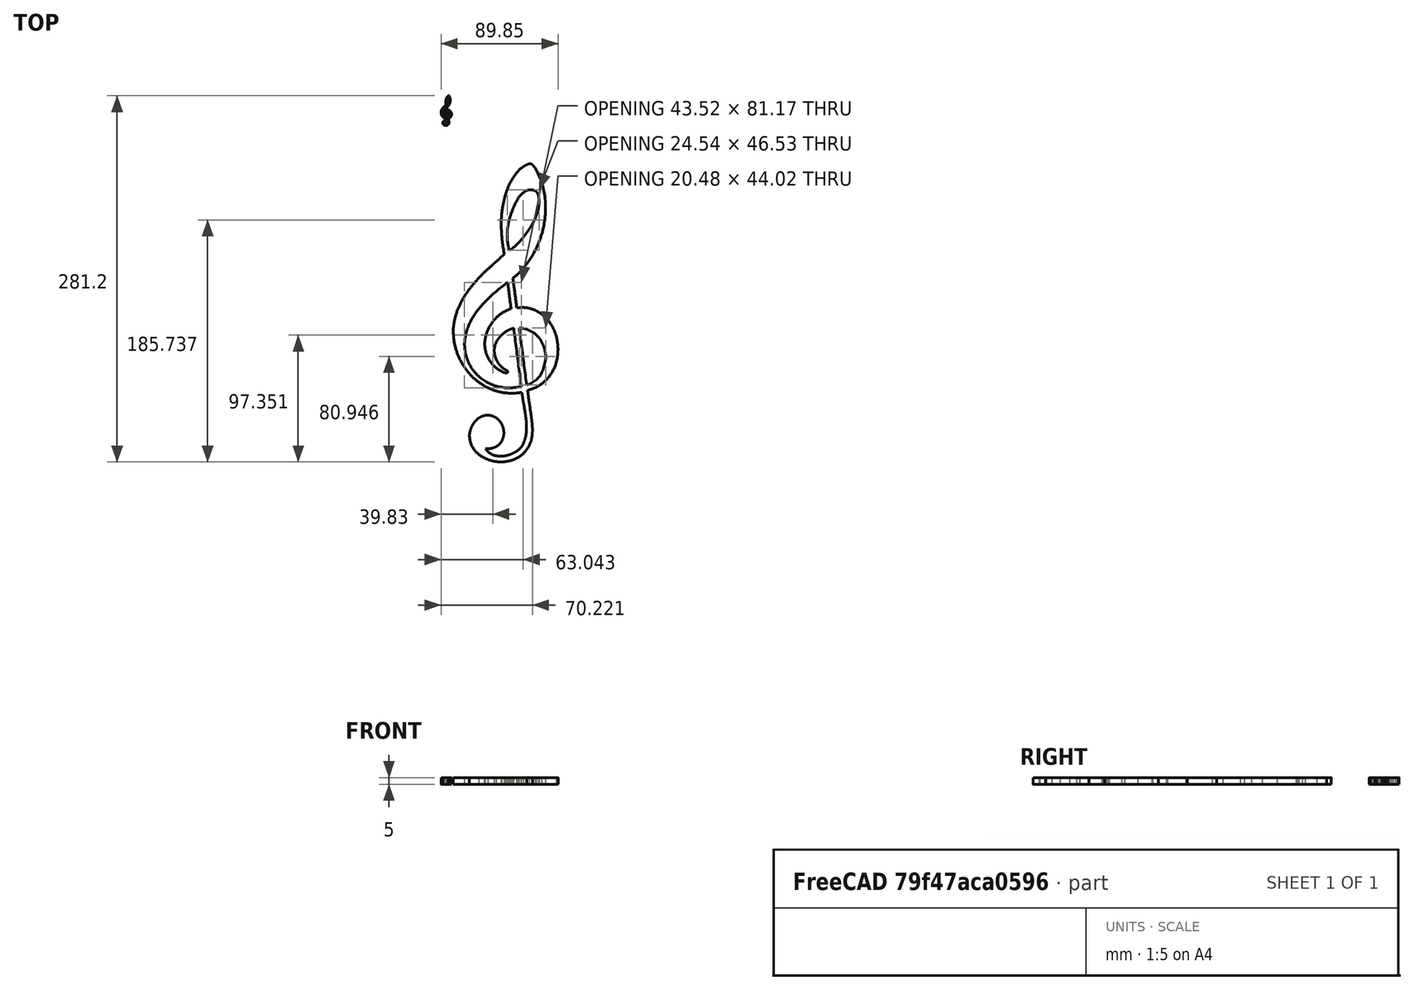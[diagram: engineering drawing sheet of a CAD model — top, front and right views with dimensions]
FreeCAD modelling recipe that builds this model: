
FCSTD DOCUMENT  (FreeCAD 0.17R13541 (Git))
Label: ClefdeSol
License: All rights reserved
LicenseURL: http://en.wikipedia.org/wiki/All_rights_reserved
objects: Part::Feature×4, Sketcher::SketchObject×2, Part::Part2DObjectPython×2, PartDesign::FeatureBase×1, PartDesign::Pad×1, PartDesign::Body×1, App::DocumentObjectGroup×1, Part::FeaturePython×1
note: 13 computed .brp shape members not serialized (recipe doc carries the construction recipe); baked Part::Feature solids carry a one-line shape summary decoded from their .brp

FEATURE [Part::Feature] path9
  shape: bbox 43.66 x 81.18 x 2e-07 mm, 1 faces, 0 solids (baked)
FEATURE [Part::Feature] path9001
  shape: bbox 20.48 x 44.02 x 2e-07 mm, 1 faces, 0 solids (baked)
FEATURE [Part::Feature] path9002
  shape: bbox 24.68 x 46.76 x 2e-07 mm, 1 faces, 0 solids (baked)
FEATURE [Part::Feature] path9003
  shape: bbox 80.9 x 229.3 x 2e-07 mm, 1 faces, 0 solids (baked)
FEATURE [Sketcher::SketchObject] Sketch
  sketch-geometry (53):
    g0: BSplineCurve PolesCount=4 KnotsCount=2 Degree=3 IsPeriodic=0
    g1: BSplineCurve PolesCount=4 KnotsCount=2 Degree=3 IsPeriodic=0
    g2: BSplineCurve PolesCount=4 KnotsCount=2 Degree=3 IsPeriodic=0
    g3: BSplineCurve PolesCount=4 KnotsCount=2 Degree=3 IsPeriodic=0
    g4: BSplineCurve PolesCount=4 KnotsCount=2 Degree=3 IsPeriodic=0
    g5: BSplineCurve PolesCount=4 KnotsCount=2 Degree=3 IsPeriodic=0
    g6: BSplineCurve PolesCount=4 KnotsCount=2 Degree=3 IsPeriodic=0
    g7: BSplineCurve PolesCount=4 KnotsCount=2 Degree=3 IsPeriodic=0
    g8: BSplineCurve PolesCount=4 KnotsCount=2 Degree=3 IsPeriodic=0
    g9: BSplineCurve PolesCount=4 KnotsCount=2 Degree=3 IsPeriodic=0
    g10: BSplineCurve PolesCount=4 KnotsCount=2 Degree=3 IsPeriodic=0
    g11: BSplineCurve PolesCount=2 KnotsCount=2 Degree=1 IsPeriodic=0
    g12: BSplineCurve PolesCount=4 KnotsCount=2 Degree=3 IsPeriodic=0
    g13: BSplineCurve PolesCount=4 KnotsCount=2 Degree=3 IsPeriodic=0
    g14: BSplineCurve PolesCount=4 KnotsCount=2 Degree=3 IsPeriodic=0
    g15: BSplineCurve PolesCount=4 KnotsCount=2 Degree=3 IsPeriodic=0
    g16: BSplineCurve PolesCount=4 KnotsCount=2 Degree=3 IsPeriodic=0
    g17: BSplineCurve PolesCount=4 KnotsCount=2 Degree=3 IsPeriodic=0
    g18: BSplineCurve PolesCount=4 KnotsCount=2 Degree=3 IsPeriodic=0
    g19: BSplineCurve PolesCount=4 KnotsCount=2 Degree=3 IsPeriodic=0
    g20: BSplineCurve PolesCount=4 KnotsCount=2 Degree=3 IsPeriodic=0
    g21: BSplineCurve PolesCount=4 KnotsCount=2 Degree=3 IsPeriodic=0
    g22: BSplineCurve PolesCount=4 KnotsCount=2 Degree=3 IsPeriodic=0
    g23: BSplineCurve PolesCount=4 KnotsCount=2 Degree=3 IsPeriodic=0
    g24: BSplineCurve PolesCount=4 KnotsCount=2 Degree=3 IsPeriodic=0
    g25: BSplineCurve PolesCount=4 KnotsCount=2 Degree=3 IsPeriodic=0
    g26: BSplineCurve PolesCount=4 KnotsCount=2 Degree=3 IsPeriodic=0
    g27: BSplineCurve PolesCount=4 KnotsCount=2 Degree=3 IsPeriodic=0
    g28: BSplineCurve PolesCount=4 KnotsCount=2 Degree=3 IsPeriodic=0
    g29: BSplineCurve PolesCount=4 KnotsCount=2 Degree=3 IsPeriodic=0
    g30: BSplineCurve PolesCount=4 KnotsCount=2 Degree=3 IsPeriodic=0
    g31: BSplineCurve PolesCount=4 KnotsCount=2 Degree=3 IsPeriodic=0
    g32: BSplineCurve PolesCount=4 KnotsCount=2 Degree=3 IsPeriodic=0
    g33: BSplineCurve PolesCount=4 KnotsCount=2 Degree=3 IsPeriodic=0
    g34: BSplineCurve PolesCount=4 KnotsCount=2 Degree=3 IsPeriodic=0
    g35: BSplineCurve PolesCount=2 KnotsCount=2 Degree=1 IsPeriodic=0
    g36: BSplineCurve PolesCount=4 KnotsCount=2 Degree=3 IsPeriodic=0
    g37: BSplineCurve PolesCount=4 KnotsCount=2 Degree=3 IsPeriodic=0
    g38: BSplineCurve PolesCount=4 KnotsCount=2 Degree=3 IsPeriodic=0
    g39: BSplineCurve PolesCount=4 KnotsCount=2 Degree=3 IsPeriodic=0
    g40: BSplineCurve PolesCount=4 KnotsCount=2 Degree=3 IsPeriodic=0
    g41: BSplineCurve PolesCount=4 KnotsCount=2 Degree=3 IsPeriodic=0
    g42: BSplineCurve PolesCount=4 KnotsCount=2 Degree=3 IsPeriodic=0
    g43: BSplineCurve PolesCount=4 KnotsCount=2 Degree=3 IsPeriodic=0
    g44: BSplineCurve PolesCount=4 KnotsCount=2 Degree=3 IsPeriodic=0
    g45: BSplineCurve PolesCount=4 KnotsCount=2 Degree=3 IsPeriodic=0
    g46: BSplineCurve PolesCount=4 KnotsCount=2 Degree=3 IsPeriodic=0
    g47: BSplineCurve PolesCount=4 KnotsCount=2 Degree=3 IsPeriodic=0
    g48: BSplineCurve PolesCount=4 KnotsCount=2 Degree=3 IsPeriodic=0
    g49: BSplineCurve PolesCount=4 KnotsCount=2 Degree=3 IsPeriodic=0
    g50: BSplineCurve PolesCount=4 KnotsCount=2 Degree=3 IsPeriodic=0
    g51: BSplineCurve PolesCount=4 KnotsCount=2 Degree=3 IsPeriodic=0
    g52: BSplineCurve PolesCount=4 KnotsCount=2 Degree=3 IsPeriodic=0
  constraints (53):
    c: Coincident(g0,g1)
    c: Coincident(g1,g2)
    c: Coincident(g2,g3)
    c: Coincident(g3,g4)
    c: Coincident(g4,g5)
    c: Coincident(g5,g6)
    c: Coincident(g6,g7)
    c: Coincident(g7,g8)
    c: Coincident(g8,g9)
    c: Coincident(g9,g10)
    c: Coincident(g10,g11)
    c: Coincident(g11,g12)
    c: Coincident(g12,g13)
    c: Coincident(g13,g14)
    c: Coincident(g14,g15)
    c: Coincident(g15,g16)
    c: Coincident(g16,g17)
    c: Coincident(g17,g18)
    c: Coincident(g18,g19)
    c: Coincident(g19,g20)
    c: Coincident(g20,g21)
    c: Coincident(g21,g22)
    c: Coincident(g22,g23)
    c: Coincident(g23,g24)
    c: Coincident(g24,g25)
    c: Coincident(g25,g26)
    c: Coincident(g26,g27)
    c: Coincident(g27,g28)
    c: Coincident(g28,g29)
    c: Coincident(g29,g30)
    c: Coincident(g30,g31)
    c: Coincident(g31,g32)
    c: Coincident(g32,g33)
    c: Coincident(g33,g34)
    c: Coincident(g34,g35)
    c: Coincident(g35,g36)
    c: Coincident(g36,g37)
    c: Coincident(g37,g38)
    c: Coincident(g38,g39)
    c: Coincident(g39,g40)
    c: Coincident(g40,g41)
    c: Coincident(g41,g42)
    c: Coincident(g42,g43)
    c: Coincident(g43,g44)
    c: Coincident(g44,g45)
    c: Coincident(g45,g46)
    c: Coincident(g46,g47)
    c: Coincident(g47,g48)
    c: Coincident(g48,g49)
    c: Coincident(g49,g50)
    c: Coincident(g50,g51)
    c: Coincident(g51,g52)
    c: Coincident(g52,g0)
FEATURE [Part::Part2DObjectPython] Block  # Draft 2D object (typed FeaturePython)
  Components = -> [Sketch,path9,path9001]
FEATURE [Part::Part2DObjectPython] Block001  # Draft 2D object (typed FeaturePython)
  Components = -> [Block,path9002]
FEATURE [Sketcher::SketchObject] Sketch001
  sketch-geometry (87):
    g0: BSplineCurve PolesCount=4 KnotsCount=2 Degree=3 IsPeriodic=0
    g1: BSplineCurve PolesCount=4 KnotsCount=2 Degree=3 IsPeriodic=0
    g2: BSplineCurve PolesCount=4 KnotsCount=2 Degree=3 IsPeriodic=0
    g3: BSplineCurve PolesCount=4 KnotsCount=2 Degree=3 IsPeriodic=0
    g4: BSplineCurve PolesCount=4 KnotsCount=2 Degree=3 IsPeriodic=0
    g5: BSplineCurve PolesCount=4 KnotsCount=2 Degree=3 IsPeriodic=0
    g6: BSplineCurve PolesCount=4 KnotsCount=2 Degree=3 IsPeriodic=0
    g7: BSplineCurve PolesCount=4 KnotsCount=2 Degree=3 IsPeriodic=0
    g8: BSplineCurve PolesCount=4 KnotsCount=2 Degree=3 IsPeriodic=0
    g9: BSplineCurve PolesCount=4 KnotsCount=2 Degree=3 IsPeriodic=0
    g10: BSplineCurve PolesCount=4 KnotsCount=2 Degree=3 IsPeriodic=0
    g11: BSplineCurve PolesCount=2 KnotsCount=2 Degree=1 IsPeriodic=0
    g12: BSplineCurve PolesCount=4 KnotsCount=2 Degree=3 IsPeriodic=0
    g13: BSplineCurve PolesCount=4 KnotsCount=2 Degree=3 IsPeriodic=0
    g14: BSplineCurve PolesCount=4 KnotsCount=2 Degree=3 IsPeriodic=0
    g15: BSplineCurve PolesCount=4 KnotsCount=2 Degree=3 IsPeriodic=0
    g16: BSplineCurve PolesCount=4 KnotsCount=2 Degree=3 IsPeriodic=0
    g17: BSplineCurve PolesCount=4 KnotsCount=2 Degree=3 IsPeriodic=0
    g18: BSplineCurve PolesCount=4 KnotsCount=2 Degree=3 IsPeriodic=0
    g19: BSplineCurve PolesCount=4 KnotsCount=2 Degree=3 IsPeriodic=0
    g20: BSplineCurve PolesCount=4 KnotsCount=2 Degree=3 IsPeriodic=0
    g21: BSplineCurve PolesCount=4 KnotsCount=2 Degree=3 IsPeriodic=0
    g22: BSplineCurve PolesCount=4 KnotsCount=2 Degree=3 IsPeriodic=0
    g23: BSplineCurve PolesCount=4 KnotsCount=2 Degree=3 IsPeriodic=0
    g24: BSplineCurve PolesCount=4 KnotsCount=2 Degree=3 IsPeriodic=0
    g25: BSplineCurve PolesCount=4 KnotsCount=2 Degree=3 IsPeriodic=0
    g26: BSplineCurve PolesCount=4 KnotsCount=2 Degree=3 IsPeriodic=0
    g27: BSplineCurve PolesCount=4 KnotsCount=2 Degree=3 IsPeriodic=0
    g28: BSplineCurve PolesCount=4 KnotsCount=2 Degree=3 IsPeriodic=0
    g29: BSplineCurve PolesCount=4 KnotsCount=2 Degree=3 IsPeriodic=0
    g30: BSplineCurve PolesCount=4 KnotsCount=2 Degree=3 IsPeriodic=0
    g31: BSplineCurve PolesCount=4 KnotsCount=2 Degree=3 IsPeriodic=0
    g32: BSplineCurve PolesCount=4 KnotsCount=2 Degree=3 IsPeriodic=0
    g33: BSplineCurve PolesCount=4 KnotsCount=2 Degree=3 IsPeriodic=0
    g34: BSplineCurve PolesCount=4 KnotsCount=2 Degree=3 IsPeriodic=0
    g35: BSplineCurve PolesCount=2 KnotsCount=2 Degree=1 IsPeriodic=0
    g36: BSplineCurve PolesCount=4 KnotsCount=2 Degree=3 IsPeriodic=0
    g37: BSplineCurve PolesCount=4 KnotsCount=2 Degree=3 IsPeriodic=0
    g38: BSplineCurve PolesCount=4 KnotsCount=2 Degree=3 IsPeriodic=0
    g39: BSplineCurve PolesCount=4 KnotsCount=2 Degree=3 IsPeriodic=0
    g40: BSplineCurve PolesCount=4 KnotsCount=2 Degree=3 IsPeriodic=0
    g41: BSplineCurve PolesCount=4 KnotsCount=2 Degree=3 IsPeriodic=0
    g42: BSplineCurve PolesCount=4 KnotsCount=2 Degree=3 IsPeriodic=0
    g43: BSplineCurve PolesCount=4 KnotsCount=2 Degree=3 IsPeriodic=0
    g44: BSplineCurve PolesCount=4 KnotsCount=2 Degree=3 IsPeriodic=0
    g45: BSplineCurve PolesCount=4 KnotsCount=2 Degree=3 IsPeriodic=0
    g46: BSplineCurve PolesCount=4 KnotsCount=2 Degree=3 IsPeriodic=0
    g47: BSplineCurve PolesCount=4 KnotsCount=2 Degree=3 IsPeriodic=0
    g48: BSplineCurve PolesCount=4 KnotsCount=2 Degree=3 IsPeriodic=0
    g49: BSplineCurve PolesCount=4 KnotsCount=2 Degree=3 IsPeriodic=0
    g50: BSplineCurve PolesCount=4 KnotsCount=2 Degree=3 IsPeriodic=0
    g51: BSplineCurve PolesCount=4 KnotsCount=2 Degree=3 IsPeriodic=0
    g52: BSplineCurve PolesCount=4 KnotsCount=2 Degree=3 IsPeriodic=0
    g53: BSplineCurve PolesCount=4 KnotsCount=2 Degree=3 IsPeriodic=0
    g54: BSplineCurve PolesCount=4 KnotsCount=2 Degree=3 IsPeriodic=0
    g55: BSplineCurve PolesCount=4 KnotsCount=2 Degree=3 IsPeriodic=0
    g56: BSplineCurve PolesCount=4 KnotsCount=2 Degree=3 IsPeriodic=0
    g57: BSplineCurve PolesCount=4 KnotsCount=2 Degree=3 IsPeriodic=0
    g58: BSplineCurve PolesCount=4 KnotsCount=2 Degree=3 IsPeriodic=0
    g59: BSplineCurve PolesCount=4 KnotsCount=2 Degree=3 IsPeriodic=0
    g60: BSplineCurve PolesCount=4 KnotsCount=2 Degree=3 IsPeriodic=0
    g61: BSplineCurve PolesCount=4 KnotsCount=2 Degree=3 IsPeriodic=0
    g62: BSplineCurve PolesCount=4 KnotsCount=2 Degree=3 IsPeriodic=0
    g63: BSplineCurve PolesCount=2 KnotsCount=2 Degree=1 IsPeriodic=0
    g64: BSplineCurve PolesCount=4 KnotsCount=2 Degree=3 IsPeriodic=0
    g65: BSplineCurve PolesCount=4 KnotsCount=2 Degree=3 IsPeriodic=0
    g66: BSplineCurve PolesCount=4 KnotsCount=2 Degree=3 IsPeriodic=0
    g67: BSplineCurve PolesCount=4 KnotsCount=2 Degree=3 IsPeriodic=0
    g68: BSplineCurve PolesCount=4 KnotsCount=2 Degree=3 IsPeriodic=0
    g69: BSplineCurve PolesCount=4 KnotsCount=2 Degree=3 IsPeriodic=0
    g70: BSplineCurve PolesCount=2 KnotsCount=2 Degree=1 IsPeriodic=0
    g71: BSplineCurve PolesCount=2 KnotsCount=2 Degree=1 IsPeriodic=0
    g72: BSplineCurve PolesCount=4 KnotsCount=2 Degree=3 IsPeriodic=0
    g73: BSplineCurve PolesCount=4 KnotsCount=2 Degree=3 IsPeriodic=0
    g74: BSplineCurve PolesCount=4 KnotsCount=2 Degree=3 IsPeriodic=0
    g75: BSplineCurve PolesCount=4 KnotsCount=2 Degree=3 IsPeriodic=0
    g76: BSplineCurve PolesCount=4 KnotsCount=2 Degree=3 IsPeriodic=0
    g77: BSplineCurve PolesCount=4 KnotsCount=2 Degree=3 IsPeriodic=0
    g78: BSplineCurve PolesCount=4 KnotsCount=2 Degree=3 IsPeriodic=0
    g79: BSplineCurve PolesCount=4 KnotsCount=2 Degree=3 IsPeriodic=0
    g80: BSplineCurve PolesCount=4 KnotsCount=2 Degree=3 IsPeriodic=0
    g81: BSplineCurve PolesCount=4 KnotsCount=2 Degree=3 IsPeriodic=0
    g82: BSplineCurve PolesCount=4 KnotsCount=2 Degree=3 IsPeriodic=0
    g83: BSplineCurve PolesCount=4 KnotsCount=2 Degree=3 IsPeriodic=0
    g84: BSplineCurve PolesCount=4 KnotsCount=2 Degree=3 IsPeriodic=0
    g85: BSplineCurve PolesCount=4 KnotsCount=2 Degree=3 IsPeriodic=0
    g86: BSplineCurve PolesCount=4 KnotsCount=2 Degree=3 IsPeriodic=0
  constraints (87):
    c: Coincident(g0,g1)
    c: Coincident(g1,g2)
    c: Coincident(g2,g3)
    c: Coincident(g3,g4)
    c: Coincident(g4,g5)
    c: Coincident(g5,g6)
    c: Coincident(g6,g7)
    c: Coincident(g7,g8)
    c: Coincident(g8,g9)
    c: Coincident(g9,g10)
    c: Coincident(g10,g11)
    c: Coincident(g11,g12)
    c: Coincident(g12,g13)
    c: Coincident(g13,g14)
    c: Coincident(g14,g15)
    c: Coincident(g15,g16)
    c: Coincident(g16,g17)
    c: Coincident(g17,g18)
    c: Coincident(g18,g19)
    c: Coincident(g19,g20)
    c: Coincident(g20,g21)
    c: Coincident(g21,g22)
    c: Coincident(g22,g23)
    c: Coincident(g23,g24)
    c: Coincident(g24,g25)
    c: Coincident(g25,g26)
    c: Coincident(g26,g27)
    c: Coincident(g27,g28)
    c: Coincident(g28,g29)
    c: Coincident(g29,g30)
    c: Coincident(g30,g31)
    c: Coincident(g31,g32)
    c: Coincident(g32,g33)
    c: Coincident(g33,g34)
    c: Coincident(g34,g35)
    c: Coincident(g35,g36)
    c: Coincident(g36,g37)
    c: Coincident(g37,g38)
    c: Coincident(g38,g39)
    c: Coincident(g39,g40)
    c: Coincident(g40,g41)
    c: Coincident(g41,g42)
    c: Coincident(g42,g43)
    c: Coincident(g43,g44)
    c: Coincident(g44,g45)
    c: Coincident(g45,g46)
    c: Coincident(g46,g47)
    c: Coincident(g47,g48)
    c: Coincident(g48,g49)
    c: Coincident(g49,g50)
    c: Coincident(g50,g51)
    c: Coincident(g51,g52)
    c: Coincident(g52,g0)
    c: Coincident(g53,g54)
    c: Coincident(g54,g55)
    c: Coincident(g55,g56)
    c: Coincident(g56,g57)
    c: Coincident(g57,g58)
    c: Coincident(g58,g59)
    c: Coincident(g59,g60)
    c: Coincident(g60,g61)
    c: Coincident(g61,g62)
    c: Coincident(g62,g63)
    c: Coincident(g63,g64)
    c: Coincident(g64,g65)
    c: Coincident(g65,g66)
    c: Coincident(g66,g67)
    c: Coincident(g67,g68)
    c: Coincident(g68,g69)
    c: Coincident(g69,g70)
    c: Coincident(g70,g53)
    c: Coincident(g71,g72)
    c: Coincident(g72,g73)
    c: Coincident(g73,g74)
    c: Coincident(g74,g75)
    c: Coincident(g75,g71)
    c: Coincident(g76,g77)
    c: Coincident(g77,g78)
    c: Coincident(g78,g79)
    c: Coincident(g79,g80)
    c: Coincident(g80,g81)
    c: Coincident(g81,g82)
    c: Coincident(g82,g83)
    c: Coincident(g83,g84)
    c: Coincident(g84,g85)
    c: Coincident(g85,g86)
    c: Coincident(g86,g76)
FEATURE [PartDesign::FeatureBase] BaseFeature
  BaseFeature = -> Block001
FEATURE [PartDesign::Pad] Pad
  BaseFeature = -> BaseFeature
  Length = 5
  Length2 = 100
  Profile = -> Sketch001
  Type = 0
FEATURE [PartDesign::Body] Body
  BaseFeature = -> Block001
  Group = -> [BaseFeature,Sketch001,Pad]
  Origin = -> Origin
  Tip = -> Pad
FEATURE [App::DocumentObjectGroup] Group  label="ClefSeSol"
  Group = -> [path9,path9001,path9002,path9003,Sketch,Block,Block001,Body]
FEATURE [Part::FeaturePython] Clone  label="Pad001"  # Draft clone (typed FeaturePython)
  AttacherType = Attacher::AttachEngine3D
  Fuse = false
  Objects = -> [Pad]
  Scale = (0.1,0.1,1)
